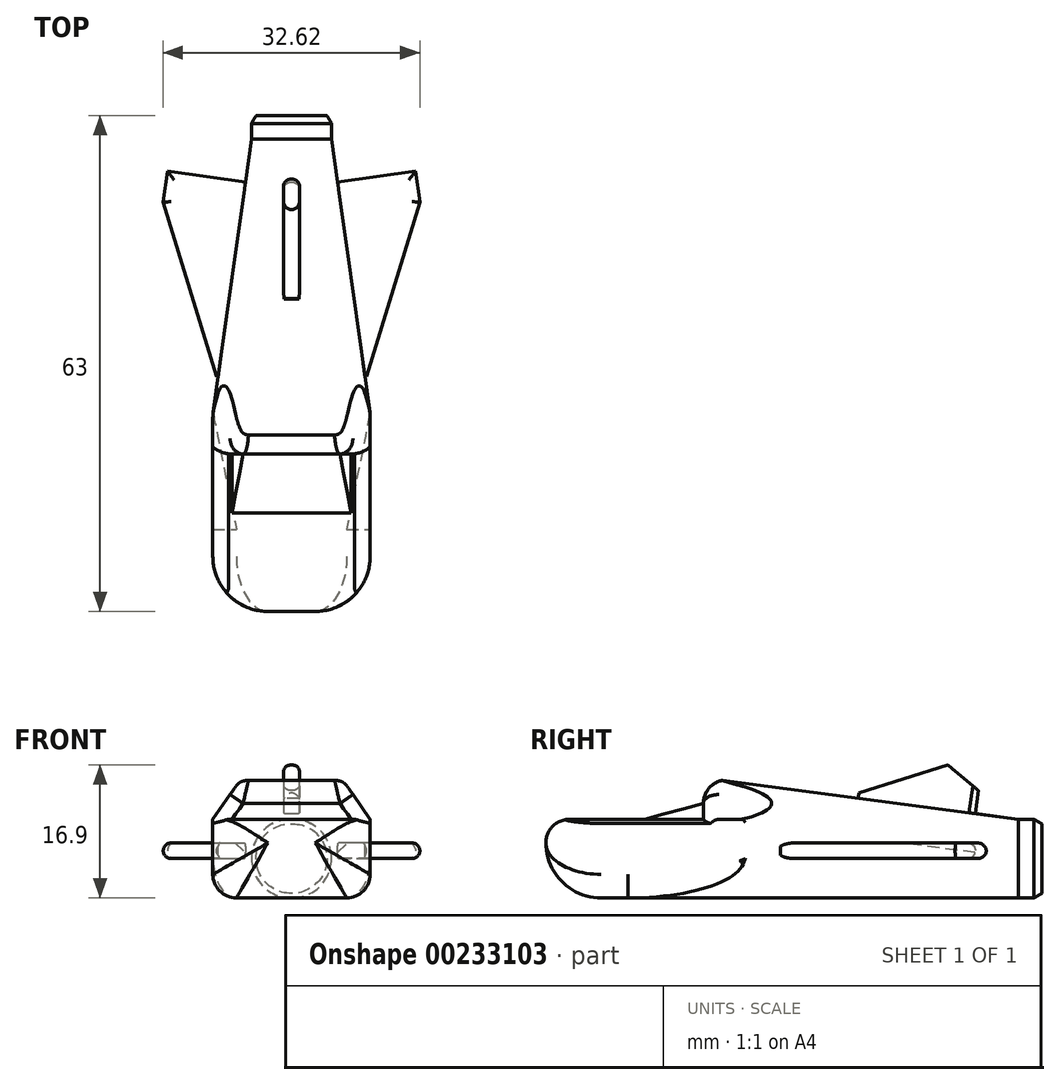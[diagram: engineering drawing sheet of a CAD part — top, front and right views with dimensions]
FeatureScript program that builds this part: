
annotation { "Feature Type Name" : "Feature", "Feature Type Description" : "" }
export const myFeature = defineFeature(function(context is Context, id is Id, definition is map)
    precondition{}
    {
        {
            var Q0;
            Q0=qCreatedBy(makeId("Right.planeOp"),FACE);
            var sketch = newSketch(context, id + "F0", { "sketchPlane" : qUnion([Q0])});
            skLineSegment(sketch, "E0", {"start": v(0, 0) * mm, "end": v(-30, 0) * mm});
            skLineSegment(sketch, "E1", {"start": v(0, 0) * mm, "end": v(30, 0) * mm});
            skLineSegment(sketch, "E2", {"start": v(30, 0) * mm, "end": v(30, -5) * mm});
            skLineSegment(sketch, "E3", {"start": v(30, 0) * mm, "end": v(30, 5) * mm});
            skLineSegment(sketch, "E4", {"start": v(-30, 0) * mm, "end": v(-30, 5) * mm});
            skLineSegment(sketch, "E5", {"start": v(-30, 0) * mm, "end": v(-30, -5) * mm});
            skLineSegment(sketch, "E6", {"start": v(30, 5) * mm, "end": v(-30, 5) * mm});
            skLineSegment(sketch, "E7", {"start": v(-30, -5) * mm, "end": v(30, -5) * mm});
            skLineSegment(sketch, "E8", {"start": v(30, 5) * mm, "end": v(30, 10) * mm});
            skLineSegment(sketch, "E9", {"start": v(30, 10) * mm, "end": v(-10, 10) * mm});
            skLineSegment(sketch, "E10", {"start": v(-10, 10) * mm, "end": v(-10, 5) * mm});
            skSolve(sketch);
        }
        {
            var Q0;
            {var subQ0=sQuery(id+"F0.wireOp",EDGE,"E8");Q0=makeQuery(id+"F0.imprint","IMPRINT",FACE,{"disambiguationData":[TD([[makeQuery(id+"F0.imprint","IMPRINT",EDGE,{"derivedFrom":subQ0}),1.0]])]});}
            var Q1;
            Q1=makeQuery(id+"F0.imprint","IMPRINT",FACE,{"disambiguationData":[TD([[makeQuery(id+"F0.imprint","IMPRINT",EDGE,{"derivedFrom":sQuery(id+"F0.wireOp",EDGE,"E0")}),-1.0]])]});
            var Q2;
            Q2=makeQuery(id+"F0.imprint","IMPRINT",FACE,{"disambiguationData":[TD([[makeQuery(id+"F0.imprint","IMPRINT",EDGE,{"derivedFrom":sQuery(id+"F0.wireOp",EDGE,"E0")}),1.0]])]});
            extrude(context, id + "F1", {"entities" : qUnion([Q0, Q1, Q2]), "depth" : 10 * mm});
        }
        {
            var Q0;
            Q0=makeQuery(id+"F1.opExtrude","CAP_FACE",FACE,{"disambiguationData":[OSD([sQuery(id+"F0.wireOp",EDGE,"E2"),sQuery(id+"F0.wireOp",EDGE,"E3"),sQuery(id+"F0.wireOp",EDGE,"E4"),sQuery(id+"F0.wireOp",EDGE,"E5"),sQuery(id+"F0.wireOp",EDGE,"E6"),sQuery(id+"F0.wireOp",EDGE,"E7"),sQuery(id+"F0.wireOp",EDGE,"E8"),sQuery(id+"F0.wireOp",EDGE,"E9"),sQuery(id+"F0.wireOp",EDGE,"E10")])],"isStart":true});
            extrude(context, id + "F2", {"entities" : qUnion([Q0]), "operationType" : NewBodyOperationType.ADD, "depth" : 10 * mm});
        }
        {
            var Q0;
            Q0=makeQuery(id+"F2.opExtrude","CAP_EDGE",EDGE,{"disambiguationData":[OSD([sQuery(id+"F0.wireOp",EDGE,"E9")])],"isStart":false});
            chamfer(context, id + "F3", {"entities" : qUnion([Q0]), "chamferType" : ChamferType.OFFSET_ANGLE, "width" : 5 * mm, "oppositeDirection" : true, "angle" : 35 * degree, "tangentPropagation" : true});
        }
        {
            var Q0;
            Q0=makeQuery(id+"F1.opExtrude","CAP_EDGE",EDGE,{"disambiguationData":[OSD([sQuery(id+"F0.wireOp",EDGE,"E9")])],"isStart":false});
            chamfer(context, id + "F4", {"entities" : qUnion([Q0]), "chamferType" : ChamferType.OFFSET_ANGLE, "width" : 5 * mm, "oppositeDirection" : false, "angle" : 35 * degree, "tangentPropagation" : true});
        }
        {
            var Q0;
            {var subQ0=sQuery(id+"F0.wireOp",EDGE,"E6");var subQ1=sQuery(id+"F0.wireOp",EDGE,"E4");Q0=makeQuery(id+"F2.boolean.opBoolean","MERGE",EDGE,{"derivedFrom":[makeQuery(id+"F1.opExtrude","SWEPT_EDGE",EDGE,{"disambiguationData":[OSD([subQ1,subQ0])]}),makeQuery(id+"F2.opExtrude","SWEPT_EDGE",EDGE,{"disambiguationData":[OSD([subQ1,subQ0])]})]});}
            var Q1;
            {var subQ0=sQuery(id+"F0.wireOp",EDGE,"E10");var subQ1=sQuery(id+"F0.wireOp",EDGE,"E9");Q1=makeQuery(id+"F2.boolean.opBoolean","MERGE",EDGE,{"derivedFrom":[makeQuery(id+"F1.opExtrude","SWEPT_EDGE",EDGE,{"disambiguationData":[OSD([subQ1,subQ0])]}),makeQuery(id+"F2.opExtrude","SWEPT_EDGE",EDGE,{"disambiguationData":[OSD([subQ1,subQ0])]})]});}
            var Q2;
            Q2=makeQuery(id+"F1.opExtrude","CAP_EDGE",EDGE,{"disambiguationData":[OSD([sQuery(id+"F0.wireOp",EDGE,"E7")])],"isStart":false});
            var Q3;
            Q3=makeQuery(id+"F2.opExtrude","CAP_EDGE",EDGE,{"disambiguationData":[OSD([sQuery(id+"F0.wireOp",EDGE,"E7")])],"isStart":false});
            fillet(context, id + "F5", {"entities" : qUnion([Q0, Q1, Q2, Q3]), "radius" : 3 * mm, "tangentPropagation" : true, "allowEdgeOverflow" : false});
        }
        {
            var Q0;
            {var subQ0=sQuery(id+"F0.wireOp",EDGE,"E10");Q0=makeQuery(id+"F3.opChamfer","BLEND_EDGE",EDGE,{"blendedFrom":[makeQuery(id+"F2.opExtrude","CAP_EDGE",EDGE,{"disambiguationData":[OSD([sQuery(id+"F0.wireOp",EDGE,"E9")])],"isStart":false}),makeQuery(id+"F2.boolean.opBoolean","MERGE",FACE,{"derivedFrom":[makeQuery(id+"F1.opExtrude","SWEPT_FACE",FACE,{"disambiguationData":[OSD([subQ0])]}),makeQuery(id+"F2.opExtrude","SWEPT_FACE",FACE,{"disambiguationData":[OSD([subQ0])]})]})],"blendedInto":[makeQuery(id+"F2.boolean.opBoolean","MERGE",FACE,{"derivedFrom":[makeQuery(id+"F1.opExtrude","SWEPT_FACE",FACE,{"disambiguationData":[OSD([subQ0])]}),makeQuery(id+"F2.opExtrude","SWEPT_FACE",FACE,{"disambiguationData":[OSD([subQ0])]})]})]});}
            var Q1;
            {var subQ0=sQuery(id+"F0.wireOp",EDGE,"E10");Q1=makeQuery(id+"F4.opChamfer","BLEND_EDGE",EDGE,{"blendedFrom":[makeQuery(id+"F1.opExtrude","CAP_EDGE",EDGE,{"disambiguationData":[OSD([sQuery(id+"F0.wireOp",EDGE,"E9")])],"isStart":false}),makeQuery(id+"F2.boolean.opBoolean","MERGE",FACE,{"derivedFrom":[makeQuery(id+"F1.opExtrude","SWEPT_FACE",FACE,{"disambiguationData":[OSD([subQ0])]}),makeQuery(id+"F2.opExtrude","SWEPT_FACE",FACE,{"disambiguationData":[OSD([subQ0])]})]})],"blendedInto":[makeQuery(id+"F2.boolean.opBoolean","MERGE",FACE,{"derivedFrom":[makeQuery(id+"F1.opExtrude","SWEPT_FACE",FACE,{"disambiguationData":[OSD([subQ0])]}),makeQuery(id+"F2.opExtrude","SWEPT_FACE",FACE,{"disambiguationData":[OSD([subQ0])]})]})]});}
            fillet(context, id + "F6", {"entities" : qUnion([Q0, Q1]), "radius" : 2 * mm, "tangentPropagation" : true, "allowEdgeOverflow" : false});
        }
        {
            var Q0;
            {var subQ0=sQuery(id+"F0.wireOp",EDGE,"E9");var subQ1=sQuery(id+"F0.wireOp",EDGE,"E8");Q0=makeQuery(id+"F2.boolean.opBoolean","MERGE",EDGE,{"derivedFrom":[makeQuery(id+"F1.opExtrude","SWEPT_EDGE",EDGE,{"disambiguationData":[OSD([subQ1,subQ0])]}),makeQuery(id+"F2.opExtrude","SWEPT_EDGE",EDGE,{"disambiguationData":[OSD([subQ1,subQ0])]})]});}
            chamfer(context, id + "F7", {"entities" : qUnion([Q0]), "chamferType" : ChamferType.OFFSET_ANGLE, "width" : 38 * mm, "oppositeDirection" : false, "angle" : 7.5 * degree});
        }
        {
            var Q0;
            Q0=makeQuery(id+"F1.opExtrude","CAP_EDGE",EDGE,{"disambiguationData":[OSD([sQuery(id+"F0.wireOp",EDGE,"E2"),sQuery(id+"F0.wireOp",EDGE,"E3"),sQuery(id+"F0.wireOp",EDGE,"E8")])],"isStart":false});
            chamfer(context, id + "F8", {"entities" : qUnion([Q0]), "chamferType" : ChamferType.OFFSET_ANGLE, "width" : 35 * mm, "oppositeDirection" : false, "angle" : 8 * degree});
        }
        {
            var Q0;
            Q0=makeQuery(id+"F2.opExtrude","CAP_EDGE",EDGE,{"disambiguationData":[OSD([sQuery(id+"F0.wireOp",EDGE,"E2"),sQuery(id+"F0.wireOp",EDGE,"E3"),sQuery(id+"F0.wireOp",EDGE,"E8")])],"isStart":false});
            chamfer(context, id + "F9", {"entities" : qUnion([Q0]), "chamferType" : ChamferType.OFFSET_ANGLE, "width" : 35 * mm, "oppositeDirection" : true, "angle" : 8 * degree});
        }
        {
            var Q0;
            {var subQ0=sQuery(id+"F0.wireOp",EDGE,"E8");Q0=makeQuery(id+"F9.opChamfer","BLEND_EDGE",EDGE,{"blendedFrom":[makeQuery(id+"F2.opExtrude","CAP_EDGE",EDGE,{"disambiguationData":[OSD([sQuery(id+"F0.wireOp",EDGE,"E2"),sQuery(id+"F0.wireOp",EDGE,"E3"),subQ0])],"isStart":false}),makeQuery(id+"F7.opChamfer","BLEND_FACE",FACE,{"disambiguationData":[OSD([subQ0,sQuery(id+"F0.wireOp",EDGE,"E9")])]})],"blendedInto":[makeQuery(id+"F7.opChamfer","BLEND_FACE",FACE,{"disambiguationData":[OSD([subQ0,sQuery(id+"F0.wireOp",EDGE,"E9")])]})]});}
            var Q1;
            {var subQ0=sQuery(id+"F0.wireOp",EDGE,"E8");Q1=makeQuery(id+"F8.opChamfer","BLEND_EDGE",EDGE,{"blendedFrom":[makeQuery(id+"F1.opExtrude","CAP_EDGE",EDGE,{"disambiguationData":[OSD([sQuery(id+"F0.wireOp",EDGE,"E2"),sQuery(id+"F0.wireOp",EDGE,"E3"),subQ0])],"isStart":false}),makeQuery(id+"F7.opChamfer","BLEND_FACE",FACE,{"disambiguationData":[OSD([subQ0,sQuery(id+"F0.wireOp",EDGE,"E9")])]})],"blendedInto":[makeQuery(id+"F7.opChamfer","BLEND_FACE",FACE,{"disambiguationData":[OSD([subQ0,sQuery(id+"F0.wireOp",EDGE,"E9")])]})]});}
            var Q2;
            {var subQ0=sQuery(id+"F0.wireOp",EDGE,"E7");Q2=makeQuery(id+"F9.opChamfer","BLEND_EDGE",EDGE,{"blendedFrom":[makeQuery(id+"F2.opExtrude","CAP_EDGE",EDGE,{"disambiguationData":[OSD([sQuery(id+"F0.wireOp",EDGE,"E2"),sQuery(id+"F0.wireOp",EDGE,"E3"),sQuery(id+"F0.wireOp",EDGE,"E8")])],"isStart":false}),makeQuery(id+"F5.opFillet","BLEND_FACE",FACE,{"disambiguationData":[OSD([subQ0]),TDD([makeQuery(id+"F2.opExtrude","CAP_EDGE",EDGE,{"disambiguationData":[OSD([subQ0])],"isStart":false})])]})],"blendedInto":[makeQuery(id+"F5.opFillet","BLEND_FACE",FACE,{"disambiguationData":[OSD([subQ0]),TDD([makeQuery(id+"F2.opExtrude","CAP_EDGE",EDGE,{"disambiguationData":[OSD([subQ0])],"isStart":false})])]})]});}
            var Q3;
            {var subQ0=sQuery(id+"F0.wireOp",EDGE,"E7");Q3=makeQuery(id+"F8.opChamfer","BLEND_EDGE",EDGE,{"blendedFrom":[makeQuery(id+"F1.opExtrude","CAP_EDGE",EDGE,{"disambiguationData":[OSD([sQuery(id+"F0.wireOp",EDGE,"E2"),sQuery(id+"F0.wireOp",EDGE,"E3"),sQuery(id+"F0.wireOp",EDGE,"E8")])],"isStart":false}),makeQuery(id+"F5.opFillet","BLEND_FACE",FACE,{"disambiguationData":[OSD([subQ0]),TDD([makeQuery(id+"F1.opExtrude","CAP_EDGE",EDGE,{"disambiguationData":[OSD([subQ0])],"isStart":false})])]})],"blendedInto":[makeQuery(id+"F5.opFillet","BLEND_FACE",FACE,{"disambiguationData":[OSD([subQ0]),TDD([makeQuery(id+"F1.opExtrude","CAP_EDGE",EDGE,{"disambiguationData":[OSD([subQ0])],"isStart":false})])]})]});}
            fillet(context, id + "F10", {"entities" : qUnion([Q0, Q1, Q2, Q3]), "radius" : 5 * mm, "tangentPropagation" : true, "allowEdgeOverflow" : false});
        }
        {
            var Q0;
            {var subQ0=sQuery(id+"F0.wireOp",EDGE,"E8");var subQ1=sQuery(id+"F0.wireOp",EDGE,"E3");var subQ2=sQuery(id+"F0.wireOp",EDGE,"E2");Q0=makeQuery(id+"F2.boolean.opBoolean","MERGE",FACE,{"derivedFrom":[makeQuery(id+"F1.opExtrude","SWEPT_FACE",FACE,{"disambiguationData":[OSD([subQ2,subQ1,subQ0])]}),makeQuery(id+"F2.opExtrude","SWEPT_FACE",FACE,{"disambiguationData":[OSD([subQ2,subQ1,subQ0])]})]});}
            extrude(context, id + "F11", {"entities" : qUnion([Q0]), "operationType" : NewBodyOperationType.ADD, "depth" : 3 * mm});
        }
        {
            var Q0;
            Q0=makeQuery(id+"F2.opExtrude","CAP_EDGE",EDGE,{"disambiguationData":[OSD([sQuery(id+"F0.wireOp",EDGE,"E4"),sQuery(id+"F0.wireOp",EDGE,"E5")])],"isStart":false});
            var Q1;
            Q1=makeQuery(id+"F1.opExtrude","CAP_EDGE",EDGE,{"disambiguationData":[OSD([sQuery(id+"F0.wireOp",EDGE,"E4"),sQuery(id+"F0.wireOp",EDGE,"E5")])],"isStart":false});
            var Q2;
            {var subQ0=sQuery(id+"F0.wireOp",EDGE,"E7");var subQ1=sQuery(id+"F0.wireOp",EDGE,"E5");Q2=makeQuery(id+"F2.boolean.opBoolean","MERGE",EDGE,{"derivedFrom":[makeQuery(id+"F1.opExtrude","SWEPT_EDGE",EDGE,{"disambiguationData":[OSD([subQ1,subQ0])]}),makeQuery(id+"F2.opExtrude","SWEPT_EDGE",EDGE,{"disambiguationData":[OSD([subQ1,subQ0])]})]});}
            fillet(context, id + "F12", {"entities" : qUnion([Q0, Q1, Q2]), "radius" : 7 * mm, "rho" : 0, "crossSection" : FilletCrossSection.CONIC, "allowEdgeOverflow" : false});
        }
        {
            var Q0;
            Q0=makeQuery(id+"F2.opExtrude","CAP_EDGE",EDGE,{"disambiguationData":[OSD([sQuery(id+"F0.wireOp",EDGE,"E6")])],"isStart":false});
            var Q1;
            Q1=makeQuery(id+"F1.opExtrude","CAP_EDGE",EDGE,{"disambiguationData":[OSD([sQuery(id+"F0.wireOp",EDGE,"E6")])],"isStart":false});
            chamfer(context, id + "F13", {"entities" : qUnion([Q0, Q1]), "chamferType" : ChamferType.OFFSET_ANGLE, "width" : 2 * mm, "oppositeDirection" : false, "angle" : 15 * degree});
        }
        {
            var Q0;
            Q0=makeQuery(id+"F7.opChamfer","BLEND_FACE",FACE,{"disambiguationData":[OSD([sQuery(id+"F0.wireOp",EDGE,"E8"),sQuery(id+"F0.wireOp",EDGE,"E9")])]});
            var sketch = newSketch(context, id + "F14", { "sketchPlane" : qUnion([Q0])});
            skLineSegment(sketch, "E11", {"start": v(0, 29.1) * mm, "end": v(0, 23.6) * mm});
            skLineSegment(sketch, "E12", {"start": v(0, 23.6) * mm, "end": v(0, 8.6) * mm, "construction": true});
            skLineSegment(sketch, "E13", {"start": v(0, 8.6) * mm, "end": v(1, 8.6) * mm});
            skLineSegment(sketch, "E14", {"start": v(0, 8.6) * mm, "end": v(-1, 8.6) * mm});
            skLineSegment(sketch, "E15", {"start": v(-1, 8.6) * mm, "end": v(-1, 23.6) * mm});
            skLineSegment(sketch, "E16", {"start": v(-1, 23.6) * mm, "end": v(0, 23.6) * mm});
            skLineSegment(sketch, "E17", {"start": v(0, 23.6) * mm, "end": v(1, 23.6) * mm});
            skLineSegment(sketch, "E18", {"start": v(1, 23.6) * mm, "end": v(1, 8.6) * mm});
            skSolve(sketch);
        }
        {
            var Q0;
            {var subQ11=sQuery(id+"F14.wireOp",EDGE,"E13");Q0=makeQuery(id+"F14.imprint","IMPRINT",FACE,{"disambiguationData":[TD([[makeQuery(id+"F14.imprint","IMPRINT",EDGE,{"derivedFrom":subQ11}),1.0]])]});}
            extrude(context, id + "F15", {"entities" : qUnion([Q0]), "operationType" : NewBodyOperationType.ADD, "depth" : 10 * mm});
        }
        {
            var Q0;
            Q0=makeQuery(id+"F15.opExtrude","CAP_EDGE",EDGE,{"disambiguationData":[OSD([sQuery(id+"F14.wireOp",EDGE,"E13"),sQuery(id+"F14.wireOp",EDGE,"E14")])],"isStart":false});
            chamfer(context, id + "F16", {"entities" : qUnion([Q0]), "chamferType" : ChamferType.OFFSET_ANGLE, "width" : 20 * mm, "oppositeDirection" : true, "angle" : 25 * degree, "tangentPropagation" : true});
        }
        {
            var Q0;
            Q0=makeQuery(id+"F16.opChamfer","BLEND_EDGE",EDGE,{"blendedFrom":[makeQuery(id+"F15.opExtrude","CAP_EDGE",EDGE,{"disambiguationData":[OSD([sQuery(id+"F14.wireOp",EDGE,"E13"),sQuery(id+"F14.wireOp",EDGE,"E14")])],"isStart":false}),makeQuery(id+"F15.opExtrude","SWEPT_FACE",FACE,{"disambiguationData":[OSD([sQuery(id+"F14.wireOp",EDGE,"E16"),sQuery(id+"F14.wireOp",EDGE,"E17")])]})],"blendedInto":[makeQuery(id+"F15.opExtrude","SWEPT_FACE",FACE,{"disambiguationData":[OSD([sQuery(id+"F14.wireOp",EDGE,"E16"),sQuery(id+"F14.wireOp",EDGE,"E17")])]})]});
            chamfer(context, id + "F17", {"entities" : qUnion([Q0]), "width" : 3 * mm, "tangentPropagation" : true});
        }
        {
            var Q0;
            {var subQ0=sQuery(id+"F0.wireOp",EDGE,"E10");Q0=makeQuery(id+"F2.boolean.opBoolean","MERGE",FACE,{"derivedFrom":[makeQuery(id+"F1.opExtrude","SWEPT_FACE",FACE,{"disambiguationData":[OSD([subQ0])]}),makeQuery(id+"F2.opExtrude","SWEPT_FACE",FACE,{"disambiguationData":[OSD([subQ0])]})]});}
            extrude(context, id + "F18", {"entities" : qUnion([Q0]), "operationType" : NewBodyOperationType.ADD, "depth" : 2.5 * mm});
        }
        {
            var Q0;
            {var subQ0=sQuery(id+"F0.wireOp",EDGE,"E10");var subQ1=sQuery(id+"F0.wireOp",EDGE,"E9");Q0=makeQuery(id+"F18.opExtrude","CAP_EDGE",EDGE,{"disambiguationData":[OSD([subQ1,subQ0]),TDD([makeQuery(id+"F5.opFillet","BLEND_EDGE",EDGE,{"blendedFrom":[makeQuery(id+"F2.boolean.opBoolean","MERGE",EDGE,{"derivedFrom":[makeQuery(id+"F1.opExtrude","SWEPT_EDGE",EDGE,{"disambiguationData":[OSD([subQ1,subQ0])]}),makeQuery(id+"F2.opExtrude","SWEPT_EDGE",EDGE,{"disambiguationData":[OSD([subQ1,subQ0])]})]}),makeQuery(id+"F2.boolean.opBoolean","MERGE",FACE,{"derivedFrom":[makeQuery(id+"F1.opExtrude","SWEPT_FACE",FACE,{"disambiguationData":[OSD([subQ0])]}),makeQuery(id+"F2.opExtrude","SWEPT_FACE",FACE,{"disambiguationData":[OSD([subQ0])]})]})],"blendedInto":[makeQuery(id+"F2.boolean.opBoolean","MERGE",FACE,{"derivedFrom":[makeQuery(id+"F1.opExtrude","SWEPT_FACE",FACE,{"disambiguationData":[OSD([subQ0])]}),makeQuery(id+"F2.opExtrude","SWEPT_FACE",FACE,{"disambiguationData":[OSD([subQ0])]})]})]})])],"isStart":false});}
            chamfer(context, id + "F19", {"entities" : qUnion([Q0]), "chamferType" : ChamferType.OFFSET_ANGLE, "width" : 2.5 * mm, "oppositeDirection" : true, "angle" : 15 * degree});
        }
        {
            var Q0;
            Q0=makeQuery(id+"F18.opExtrude","CAP_FACE",FACE,{"disambiguationData":[OSD([sQuery(id+"F0.wireOp",EDGE,"E10")])],"isStart":false});
            extrude(context, id + "F20", {"entities" : qUnion([Q0]), "operationType" : NewBodyOperationType.ADD, "depth" : 2.5 * mm});
        }
        {
            var Q0;
            {var subQ0=sQuery(id+"F0.wireOp",EDGE,"E10");var subQ1=sQuery(id+"F0.wireOp",EDGE,"E9");Q0=makeQuery(id+"F20.opExtrude","CAP_EDGE",EDGE,{"disambiguationData":[OSD([subQ1,subQ0]),TDD([makeQuery(id+"F19.opChamfer","BLEND_EDGE",EDGE,{"blendedFrom":[makeQuery(id+"F18.opExtrude","CAP_EDGE",EDGE,{"disambiguationData":[OSD([subQ1,subQ0]),TDD([makeQuery(id+"F5.opFillet","BLEND_EDGE",EDGE,{"blendedFrom":[makeQuery(id+"F2.boolean.opBoolean","MERGE",EDGE,{"derivedFrom":[makeQuery(id+"F1.opExtrude","SWEPT_EDGE",EDGE,{"disambiguationData":[OSD([subQ1,subQ0])]}),makeQuery(id+"F2.opExtrude","SWEPT_EDGE",EDGE,{"disambiguationData":[OSD([subQ1,subQ0])]})]}),makeQuery(id+"F2.boolean.opBoolean","MERGE",FACE,{"derivedFrom":[makeQuery(id+"F1.opExtrude","SWEPT_FACE",FACE,{"disambiguationData":[OSD([subQ0])]}),makeQuery(id+"F2.opExtrude","SWEPT_FACE",FACE,{"disambiguationData":[OSD([subQ0])]})]})],"blendedInto":[makeQuery(id+"F2.boolean.opBoolean","MERGE",FACE,{"derivedFrom":[makeQuery(id+"F1.opExtrude","SWEPT_FACE",FACE,{"disambiguationData":[OSD([subQ0])]}),makeQuery(id+"F2.opExtrude","SWEPT_FACE",FACE,{"disambiguationData":[OSD([subQ0])]})]})]})])],"isStart":false}),makeQuery(id+"F18.opExtrude","CAP_FACE",FACE,{"disambiguationData":[OSD([subQ0])],"isStart":false})],"blendedInto":[makeQuery(id+"F18.opExtrude","CAP_FACE",FACE,{"disambiguationData":[OSD([subQ0])],"isStart":false})]})])],"isStart":false});}
            chamfer(context, id + "F21", {"entities" : qUnion([Q0]), "chamferType" : ChamferType.OFFSET_ANGLE, "width" : 2.5 * mm, "oppositeDirection" : true, "angle" : 15 * degree, "tangentPropagation" : true});
        }
        {
            var Q0;
            Q0=makeQuery(id+"F20.opExtrude","CAP_FACE",FACE,{"disambiguationData":[OSD([sQuery(id+"F0.wireOp",EDGE,"E10")])],"isStart":false});
            extrude(context, id + "F22", {"entities" : qUnion([Q0]), "operationType" : NewBodyOperationType.ADD, "depth" : 2.5 * mm});
        }
        {
            var Q0;
            {var subQ0=sQuery(id+"F0.wireOp",EDGE,"E10");var subQ1=sQuery(id+"F0.wireOp",EDGE,"E9");Q0=makeQuery(id+"F22.opExtrude","CAP_EDGE",EDGE,{"disambiguationData":[OSD([subQ1,subQ0]),TDD([makeQuery(id+"F21.opChamfer","BLEND_EDGE",EDGE,{"blendedFrom":[makeQuery(id+"F20.opExtrude","CAP_EDGE",EDGE,{"disambiguationData":[OSD([subQ1,subQ0]),TDD([makeQuery(id+"F19.opChamfer","BLEND_EDGE",EDGE,{"blendedFrom":[makeQuery(id+"F18.opExtrude","CAP_EDGE",EDGE,{"disambiguationData":[OSD([subQ1,subQ0]),TDD([makeQuery(id+"F5.opFillet","BLEND_EDGE",EDGE,{"blendedFrom":[makeQuery(id+"F2.boolean.opBoolean","MERGE",EDGE,{"derivedFrom":[makeQuery(id+"F1.opExtrude","SWEPT_EDGE",EDGE,{"disambiguationData":[OSD([subQ1,subQ0])]}),makeQuery(id+"F2.opExtrude","SWEPT_EDGE",EDGE,{"disambiguationData":[OSD([subQ1,subQ0])]})]}),makeQuery(id+"F2.boolean.opBoolean","MERGE",FACE,{"derivedFrom":[makeQuery(id+"F1.opExtrude","SWEPT_FACE",FACE,{"disambiguationData":[OSD([subQ0])]}),makeQuery(id+"F2.opExtrude","SWEPT_FACE",FACE,{"disambiguationData":[OSD([subQ0])]})]})],"blendedInto":[makeQuery(id+"F2.boolean.opBoolean","MERGE",FACE,{"derivedFrom":[makeQuery(id+"F1.opExtrude","SWEPT_FACE",FACE,{"disambiguationData":[OSD([subQ0])]}),makeQuery(id+"F2.opExtrude","SWEPT_FACE",FACE,{"disambiguationData":[OSD([subQ0])]})]})]})])],"isStart":false}),makeQuery(id+"F18.opExtrude","CAP_FACE",FACE,{"disambiguationData":[OSD([subQ0])],"isStart":false})],"blendedInto":[makeQuery(id+"F18.opExtrude","CAP_FACE",FACE,{"disambiguationData":[OSD([subQ0])],"isStart":false})]})])],"isStart":false}),makeQuery(id+"F20.opExtrude","CAP_FACE",FACE,{"disambiguationData":[OSD([subQ0])],"isStart":false})],"blendedInto":[makeQuery(id+"F20.opExtrude","CAP_FACE",FACE,{"disambiguationData":[OSD([subQ0])],"isStart":false})]})])],"isStart":false});}
            chamfer(context, id + "F23", {"entities" : qUnion([Q0]), "chamferType" : ChamferType.OFFSET_ANGLE, "width" : 2.5 * mm, "oppositeDirection" : true, "angle" : 15 * degree, "tangentPropagation" : true});
        }
        {
            var Q0;
            Q0=makeQuery(id+"F9.opChamfer","BLEND_FACE",FACE,{"disambiguationData":[OSD([sQuery(id+"F0.wireOp",EDGE,"E2"),sQuery(id+"F0.wireOp",EDGE,"E3"),sQuery(id+"F0.wireOp",EDGE,"E8")])]});
            var sketch = newSketch(context, id + "F24", { "sketchPlane" : qUnion([Q0])});
            skLineSegment(sketch, "E19", {"start": v(-29, 0.05) * mm, "end": v(-23.5, 0) * mm});
            skLineSegment(sketch, "E20", {"start": v(-23.5, 0) * mm, "end": v(1.5, 0) * mm});
            skLineSegment(sketch, "E21", {"start": v(1.5, 0) * mm, "end": v(1.5, 2) * mm});
            skLineSegment(sketch, "E22", {"start": v(1.5, 2) * mm, "end": v(-23.5, 2) * mm});
            skLineSegment(sketch, "E23", {"start": v(-23.5, 2) * mm, "end": v(-23.5, 0) * mm});
            skSolve(sketch);
        }
        {
            var Q0;
            {var subQ1=sQuery(id+"F24.wireOp",EDGE,"E20");Q0=makeQuery(id+"F24.imprint","IMPRINT",FACE,{"disambiguationData":[TD([[makeQuery(id+"F24.imprint","IMPRINT",EDGE,{"derivedFrom":subQ1}),1.0]])]});}
            var Q1;
            {var subQ0=sQuery(id+"F24.wireOp",EDGE,"E23");var subQ1=sQuery(id+"F24.wireOp",EDGE,"E22");var subQ2=makeQuery(id+"F24.imprint","INTERSECT",VERTEX,{"derivedFrom":[subQ1,subQ0]});Q1=makeQuery(id+"F24.imprint","IMPRINT",FACE,{"disambiguationData":[TD([[makeQuery(id+"F24.imprint","IMPRINT",EDGE,{"disambiguationData":[TD([[subQ2,1.0]])],"derivedFrom":subQ1}),1.0]])]});}
            extrude(context, id + "F25", {"entities" : qUnion([Q0, Q1]), "operationType" : NewBodyOperationType.ADD, "depth" : 10 * mm});
        }
        {
            var Q0;
            Q0=makeQuery(id+"F8.opChamfer","BLEND_FACE",FACE,{"disambiguationData":[OSD([sQuery(id+"F0.wireOp",EDGE,"E2"),sQuery(id+"F0.wireOp",EDGE,"E3"),sQuery(id+"F0.wireOp",EDGE,"E8")])]});
            var sketch = newSketch(context, id + "F26", { "sketchPlane" : qUnion([Q0])});
            skLineSegment(sketch, "E24", {"start": v(29, 0.05) * mm, "end": v(23.5, 0) * mm});
            skLineSegment(sketch, "E25", {"start": v(23.5, 0) * mm, "end": v(-1.5, 0) * mm});
            skLineSegment(sketch, "E26", {"start": v(-1.5, 0) * mm, "end": v(-1.5, 2) * mm});
            skLineSegment(sketch, "E27", {"start": v(-1.5, 2) * mm, "end": v(23.5, 2) * mm});
            skLineSegment(sketch, "E28", {"start": v(23.5, 2) * mm, "end": v(23.5, 0) * mm});
            skSolve(sketch);
        }
        {
            var Q0;
            {var subQ2=sQuery(id+"F26.wireOp",EDGE,"E25");Q0=makeQuery(id+"F26.imprint","IMPRINT",FACE,{"disambiguationData":[TD([[makeQuery(id+"F26.imprint","IMPRINT",EDGE,{"derivedFrom":subQ2}),1.0]])]});}
            var Q1;
            {var subQ0=sQuery(id+"F26.wireOp",EDGE,"E28");var subQ1=sQuery(id+"F26.wireOp",EDGE,"E27");var subQ2=makeQuery(id+"F26.imprint","INTERSECT",VERTEX,{"derivedFrom":[subQ1,subQ0]});Q1=makeQuery(id+"F26.imprint","IMPRINT",FACE,{"disambiguationData":[TD([[makeQuery(id+"F26.imprint","IMPRINT",EDGE,{"disambiguationData":[TD([[subQ2,1.0]])],"derivedFrom":subQ1}),-1.0]])]});}
            extrude(context, id + "F27", {"entities" : qUnion([Q0, Q1]), "operationType" : NewBodyOperationType.ADD, "depth" : 10 * mm});
        }
        {
            var Q0;
            Q0=makeQuery(id+"F25.opExtrude","CAP_EDGE",EDGE,{"disambiguationData":[OSD([sQuery(id+"F24.wireOp",EDGE,"E21")])],"isStart":false});
            chamfer(context, id + "F28", {"entities" : qUnion([Q0]), "chamferType" : ChamferType.OFFSET_ANGLE, "width" : 21 * mm, "oppositeDirection" : false, "angle" : 25 * degree, "tangentPropagation" : true});
        }
        {
            var Q0;
            Q0=makeQuery(id+"F27.opExtrude","CAP_EDGE",EDGE,{"disambiguationData":[OSD([sQuery(id+"F26.wireOp",EDGE,"E26")])],"isStart":false});
            chamfer(context, id + "F29", {"entities" : qUnion([Q0]), "chamferType" : ChamferType.OFFSET_ANGLE, "width" : 21 * mm, "oppositeDirection" : true, "angle" : 25 * degree, "tangentPropagation" : true});
        }
        {
            var Q0;
            Q0=makeQuery(id+"F28.opChamfer","BLEND_EDGE",EDGE,{"blendedFrom":[makeQuery(id+"F25.opExtrude","CAP_EDGE",EDGE,{"disambiguationData":[OSD([sQuery(id+"F24.wireOp",EDGE,"E21")])],"isStart":false}),makeQuery(id+"F25.opExtrude","SWEPT_FACE",FACE,{"disambiguationData":[OSD([sQuery(id+"F24.wireOp",EDGE,"E22")])]})],"blendedInto":[makeQuery(id+"F25.opExtrude","SWEPT_FACE",FACE,{"disambiguationData":[OSD([sQuery(id+"F24.wireOp",EDGE,"E22")])]})]});
            var Q1;
            Q1=makeQuery(id+"F28.opChamfer","BLEND_EDGE",EDGE,{"blendedFrom":[makeQuery(id+"F25.opExtrude","CAP_EDGE",EDGE,{"disambiguationData":[OSD([sQuery(id+"F24.wireOp",EDGE,"E21")])],"isStart":false}),makeQuery(id+"F25.opExtrude","SWEPT_FACE",FACE,{"disambiguationData":[OSD([sQuery(id+"F24.wireOp",EDGE,"E20")])]})],"blendedInto":[makeQuery(id+"F25.opExtrude","SWEPT_FACE",FACE,{"disambiguationData":[OSD([sQuery(id+"F24.wireOp",EDGE,"E20")])]})]});
            fillet(context, id + "F30", {"entities" : qUnion([Q0, Q1]), "radius" : 1 * mm, "allowEdgeOverflow" : false});
        }
        {
            var Q0;
            Q0=makeQuery(id+"F25.opExtrude","CAP_EDGE",EDGE,{"disambiguationData":[OSD([sQuery(id+"F24.wireOp",EDGE,"E22")])],"isStart":false});
            var Q1;
            Q1=makeQuery(id+"F25.opExtrude","CAP_EDGE",EDGE,{"disambiguationData":[OSD([sQuery(id+"F24.wireOp",EDGE,"E20")])],"isStart":false});
            var Q2;
            Q2=makeQuery(id+"F25.opExtrude","SWEPT_EDGE",EDGE,{"disambiguationData":[OSD([sQuery(id+"F24.wireOp",EDGE,"E22"),sQuery(id+"F24.wireOp",EDGE,"E23")])]});
            var Q3;
            Q3=makeQuery(id+"F25.opExtrude","SWEPT_EDGE",EDGE,{"disambiguationData":[OSD([sQuery(id+"F0.wireOp",EDGE,"E2"),sQuery(id+"F0.wireOp",EDGE,"E3"),sQuery(id+"F0.wireOp",EDGE,"E7"),sQuery(id+"F0.wireOp",EDGE,"E8"),sQuery(id+"F24.wireOp",EDGE,"E19"),sQuery(id+"F24.wireOp",EDGE,"E20"),sQuery(id+"F24.wireOp",EDGE,"E23")])]});
            var Q4;
            Q4=makeQuery(id+"F29.opChamfer","BLEND_EDGE",EDGE,{"blendedFrom":[makeQuery(id+"F27.opExtrude","CAP_EDGE",EDGE,{"disambiguationData":[OSD([sQuery(id+"F26.wireOp",EDGE,"E26")])],"isStart":false}),makeQuery(id+"F27.opExtrude","SWEPT_FACE",FACE,{"disambiguationData":[OSD([sQuery(id+"F26.wireOp",EDGE,"E27")])]})],"blendedInto":[makeQuery(id+"F27.opExtrude","SWEPT_FACE",FACE,{"disambiguationData":[OSD([sQuery(id+"F26.wireOp",EDGE,"E27")])]})]});
            var Q5;
            Q5=makeQuery(id+"F29.opChamfer","BLEND_EDGE",EDGE,{"blendedFrom":[makeQuery(id+"F27.opExtrude","CAP_EDGE",EDGE,{"disambiguationData":[OSD([sQuery(id+"F26.wireOp",EDGE,"E26")])],"isStart":false}),makeQuery(id+"F27.opExtrude","SWEPT_FACE",FACE,{"disambiguationData":[OSD([sQuery(id+"F26.wireOp",EDGE,"E25")])]})],"blendedInto":[makeQuery(id+"F27.opExtrude","SWEPT_FACE",FACE,{"disambiguationData":[OSD([sQuery(id+"F26.wireOp",EDGE,"E25")])]})]});
            var Q6;
            Q6=makeQuery(id+"F27.opExtrude","CAP_EDGE",EDGE,{"disambiguationData":[OSD([sQuery(id+"F26.wireOp",EDGE,"E27")])],"isStart":false});
            var Q7;
            Q7=makeQuery(id+"F27.opExtrude","CAP_EDGE",EDGE,{"disambiguationData":[OSD([sQuery(id+"F26.wireOp",EDGE,"E25")])],"isStart":false});
            var Q8;
            Q8=makeQuery(id+"F27.opExtrude","SWEPT_EDGE",EDGE,{"disambiguationData":[OSD([sQuery(id+"F26.wireOp",EDGE,"E27"),sQuery(id+"F26.wireOp",EDGE,"E28")])]});
            var Q9;
            Q9=makeQuery(id+"F27.opExtrude","SWEPT_EDGE",EDGE,{"disambiguationData":[OSD([sQuery(id+"F0.wireOp",EDGE,"E2"),sQuery(id+"F0.wireOp",EDGE,"E3"),sQuery(id+"F0.wireOp",EDGE,"E7"),sQuery(id+"F0.wireOp",EDGE,"E8"),sQuery(id+"F26.wireOp",EDGE,"E24"),sQuery(id+"F26.wireOp",EDGE,"E25"),sQuery(id+"F26.wireOp",EDGE,"E28")])]});
            fillet(context, id + "F31", {"entities" : qUnion([Q0, Q1, Q2, Q3, Q4, Q5, Q6, Q7, Q8, Q9]), "radius" : 1 * mm, "allowEdgeOverflow" : false});
        }
        {
            var Q0;
            Q0=makeQuery(id+"F16.opChamfer","BLEND_EDGE",EDGE,{"blendedFrom":[makeQuery(id+"F15.opExtrude","CAP_EDGE",EDGE,{"disambiguationData":[OSD([sQuery(id+"F14.wireOp",EDGE,"E13"),sQuery(id+"F14.wireOp",EDGE,"E14")])],"isStart":false}),makeQuery(id+"F15.opExtrude","SWEPT_FACE",FACE,{"disambiguationData":[OSD([sQuery(id+"F14.wireOp",EDGE,"E15")])]})],"blendedInto":[makeQuery(id+"F15.opExtrude","SWEPT_FACE",FACE,{"disambiguationData":[OSD([sQuery(id+"F14.wireOp",EDGE,"E15")])]})]});
            var Q1;
            Q1=makeQuery(id+"F16.opChamfer","BLEND_EDGE",EDGE,{"blendedFrom":[makeQuery(id+"F15.opExtrude","CAP_EDGE",EDGE,{"disambiguationData":[OSD([sQuery(id+"F14.wireOp",EDGE,"E13"),sQuery(id+"F14.wireOp",EDGE,"E14")])],"isStart":false}),makeQuery(id+"F15.opExtrude","SWEPT_FACE",FACE,{"disambiguationData":[OSD([sQuery(id+"F14.wireOp",EDGE,"E18")])]})],"blendedInto":[makeQuery(id+"F15.opExtrude","SWEPT_FACE",FACE,{"disambiguationData":[OSD([sQuery(id+"F14.wireOp",EDGE,"E18")])]})]});
            var Q2;
            Q2=makeQuery(id+"F15.opExtrude","SWEPT_EDGE",EDGE,{"disambiguationData":[OSD([sQuery(id+"F0.wireOp",EDGE,"E2"),sQuery(id+"F0.wireOp",EDGE,"E3"),sQuery(id+"F0.wireOp",EDGE,"E8"),sQuery(id+"F0.wireOp",EDGE,"E9"),sQuery(id+"F14.wireOp",EDGE,"E16")])]});
            var Q3;
            Q3=makeQuery(id+"F15.opExtrude","SWEPT_EDGE",EDGE,{"disambiguationData":[OSD([sQuery(id+"F0.wireOp",EDGE,"E2"),sQuery(id+"F0.wireOp",EDGE,"E3"),sQuery(id+"F0.wireOp",EDGE,"E8"),sQuery(id+"F0.wireOp",EDGE,"E9"),sQuery(id+"F14.wireOp",EDGE,"E17")])]});
            fillet(context, id + "F32", {"entities" : qUnion([Q0, Q1, Q2, Q3]), "radius" : 1 * mm, "tangentPropagation" : true, "allowEdgeOverflow" : false});
        }
        {
            var Q0;
            {var subQ0=sQuery(id+"F0.wireOp",EDGE,"E8");var subQ1=sQuery(id+"F0.wireOp",EDGE,"E3");var subQ2=sQuery(id+"F0.wireOp",EDGE,"E2");var subQ3=sQuery(id+"F0.wireOp",EDGE,"E9");Q0=makeQuery(id+"F11.opExtrude","CAP_EDGE",EDGE,{"disambiguationData":[OSD([subQ2,subQ1,subQ0,subQ3]),TDD([makeQuery(id+"F10.opFillet","BLEND_EDGE",EDGE,{"blendedFrom":[makeQuery(id+"F9.opChamfer","BLEND_EDGE",EDGE,{"blendedFrom":[makeQuery(id+"F2.opExtrude","CAP_EDGE",EDGE,{"disambiguationData":[OSD([subQ2,subQ1,subQ0])],"isStart":false}),makeQuery(id+"F7.opChamfer","BLEND_FACE",FACE,{"disambiguationData":[OSD([subQ0,subQ3])]})],"blendedInto":[makeQuery(id+"F7.opChamfer","BLEND_FACE",FACE,{"disambiguationData":[OSD([subQ0,subQ3])]})]}),makeQuery(id+"F2.boolean.opBoolean","MERGE",FACE,{"derivedFrom":[makeQuery(id+"F1.opExtrude","SWEPT_FACE",FACE,{"disambiguationData":[OSD([subQ2,subQ1,subQ0])]}),makeQuery(id+"F2.opExtrude","SWEPT_FACE",FACE,{"disambiguationData":[OSD([subQ2,subQ1,subQ0])]})]})],"blendedInto":[makeQuery(id+"F2.boolean.opBoolean","MERGE",FACE,{"derivedFrom":[makeQuery(id+"F1.opExtrude","SWEPT_FACE",FACE,{"disambiguationData":[OSD([subQ2,subQ1,subQ0])]}),makeQuery(id+"F2.opExtrude","SWEPT_FACE",FACE,{"disambiguationData":[OSD([subQ2,subQ1,subQ0])]})]})]})])],"isStart":false});}
            chamfer(context, id + "F33", {"entities" : qUnion([Q0]), "chamferType" : ChamferType.OFFSET_ANGLE, "width" : 1 * mm, "oppositeDirection" : true, "angle" : 30 * degree, "tangentPropagation" : true});
        }
    });
